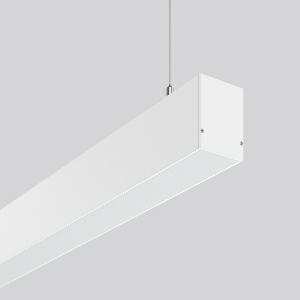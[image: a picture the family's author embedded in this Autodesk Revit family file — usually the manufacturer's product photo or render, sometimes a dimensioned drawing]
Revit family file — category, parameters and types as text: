
# Revit family: less_is_more_50_312312_002_76_6ccb
name_source: partatom
category: Lighting Fixtures
units: mm (PartAtom-declared; Revit-internal decimal feet)

## family parameters
Cut with Voids When Loaded = No
Host = Face
Light Source = No
Part Type = Normal
Room Calculation Point = No
Round Connector Dimension = Use Diameter
Shared = No

## types (1)
- LESS IS MORE 50 (1 x LED Modul 830, 3100 lm, 3000)
    Apparent Load = 28 VA
    CIE Flux Codes = 48 79 95 100 100
    Color Rendering = 80
    Color Temperature = 3000
    Default Elevation = 1800 mm
    Description = Series: LESS IS MORE 50
Linear pendant luminaire for aesthetically sophisticated lighting. Housing: extruded aluminium profile, powder-coated. End cap aluminium powder-coated. Canopy made of aluminium, powder-coated. Diffuser made of non-yellowing plastic (PMMA), opal. Direct light emission. Suitable for pendant. 2-point steel cable suspension freely positionable and infinitely height-adjustable. Special lengths available on request. LED unit with integrated converter interchangeable and removable. Suitable for through-wiring. With sensors or as a safety luminaire on request. 
Colour: traffic white, matt (RAL 9016)
Length: 1127 mm
Width: 57 mm
Height: 75 mm
Suspension length: 2000 mm
Lamp: LED
Socket: without socket
Colour temperature: 3000K
Colour rendering index (CRI): 80
System power: 28 W
Rated luminous flux: 3100 lm
Luminous efficiency: 111 lm/W
Control gear: Converter, dimmable, DALI
Protection class: I
Type of protection: IP 20
    Height = 75 mm
    Lamp = 1 x LED Modul 830
    Lamp Light Flux = 3100 lm
    Lamp count = 1
    Length = 1127 mm
    Lifetime = 50000 h
    Luminous efficacy = 111 lm/W
    Manufacturer = RZB
    ModVariant = No
    Model = 312312.002.76
    Mounting Place = Ceiling
    Mounting Type = Pendant
    Number of Poles = 1
    OnlyDefault = Yes
    Power Factor = 1
    Product Name = LESS IS MORE 50
    Product group = Pendant LED linear luminaires
    ProductGroupID = 907
    Protection Class = Protection class I
    Protection Degree = IP 20
    RLX_Detail_Level = 1
    RLX_Emergency_Light_Flux = 0 lm
    RLX_Emergency_Type = 0
    RLX_Emergency_Type_DB = No
    RlxData = <blob elided: 20617 chars, md5=a292febe>
    Socket = socket
    Standby Power = 0 W
    System Light Flux = 3100 lm
    System Power = 28 W
    Type Comments = Product without accessories
    Type Image = 312318.002.jpg
    URL = http://relux.com
    VarID = ---
    Voltage = 230 V
    Voltage Range = 220-240 V
    Weight = 0.00 kg
    Width = 57 mm

## geometry (parser evidence)
native form markers: Blend x4, Sweep x11
no freeform markers — native parametric forms only
